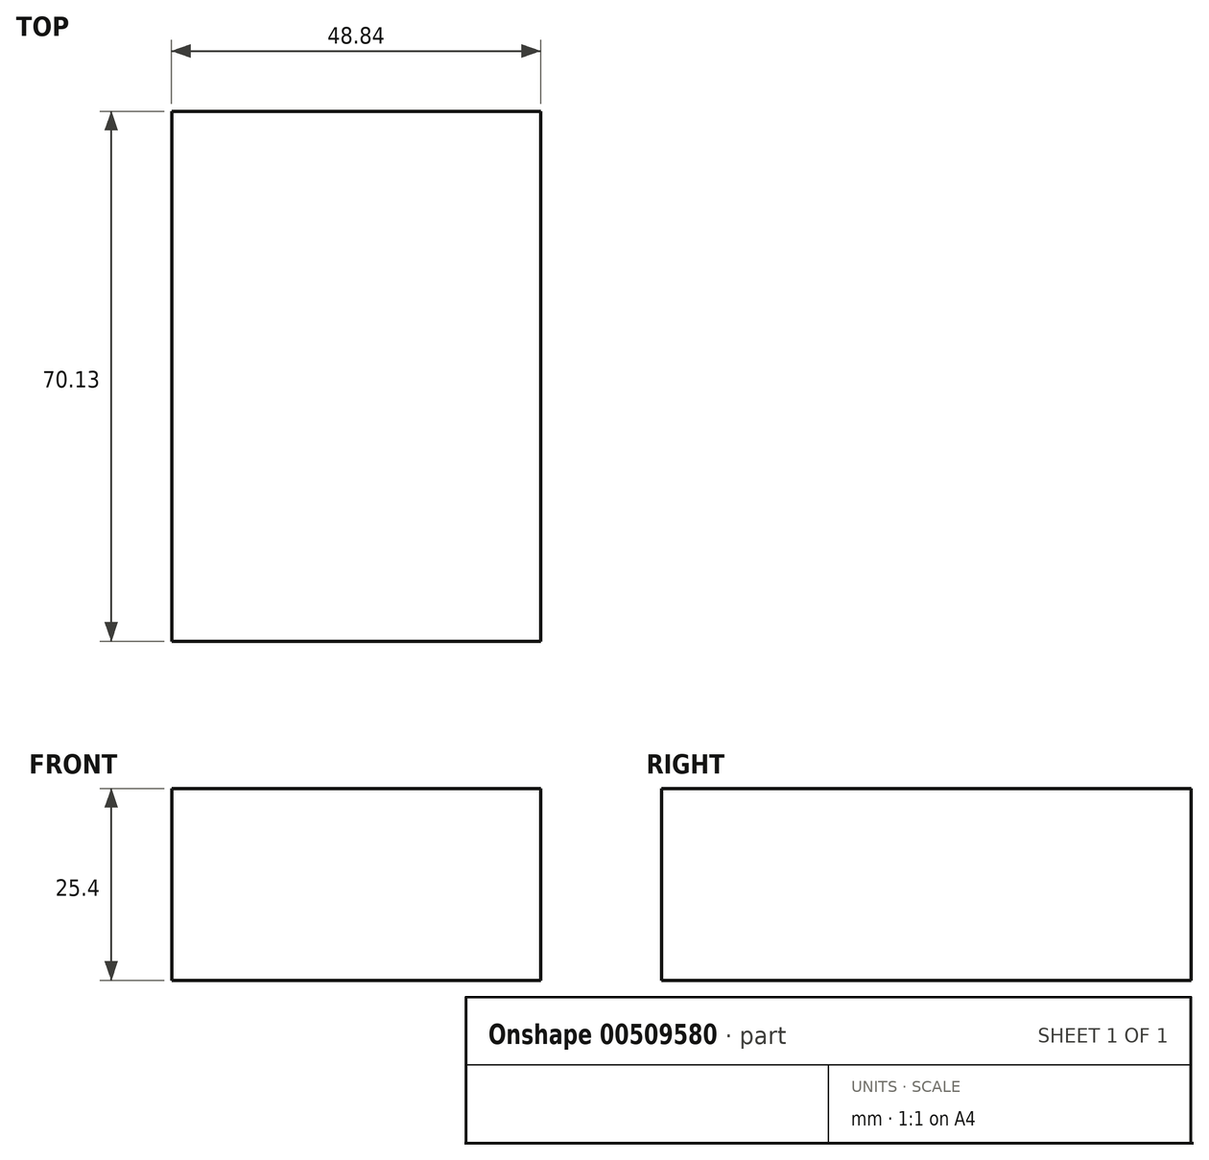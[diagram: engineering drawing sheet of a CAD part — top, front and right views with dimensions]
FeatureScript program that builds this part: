
annotation { "Feature Type Name" : "Feature", "Feature Type Description" : "" }
export const myFeature = defineFeature(function(context is Context, id is Id, definition is map)
    precondition{}
    {
        {
            var Q0;
            Q0=qCreatedBy(makeId("Top.planeOp"),FACE);
            var sketch = newSketch(context, id + "F0", { "sketchPlane" : qUnion([Q0])});
            skLineSegment(sketch, "E0.bottom", {"start": v(-64.55, -50.03) * mm, "end": v(-15.7, -50.03) * mm});
            skLineSegment(sketch, "E0.top", {"start": v(-64.55, 20.1) * mm, "end": v(-15.7, 20.1) * mm});
            skLineSegment(sketch, "E0.left", {"start": v(-64.55, -50.03) * mm, "end": v(-64.55, 20.1) * mm});
            skLineSegment(sketch, "E0.right", {"start": v(-15.7, -50.03) * mm, "end": v(-15.7, 20.1) * mm});
            skSolve(sketch);
        }
        {
            var Q0;
            Q0 = qSketchRegion(id + "F0", true);
            extrude(context, id + "F1", {"entities" : qUnion([Q0]), "depth" : 25.4 * mm});
        }
    });
